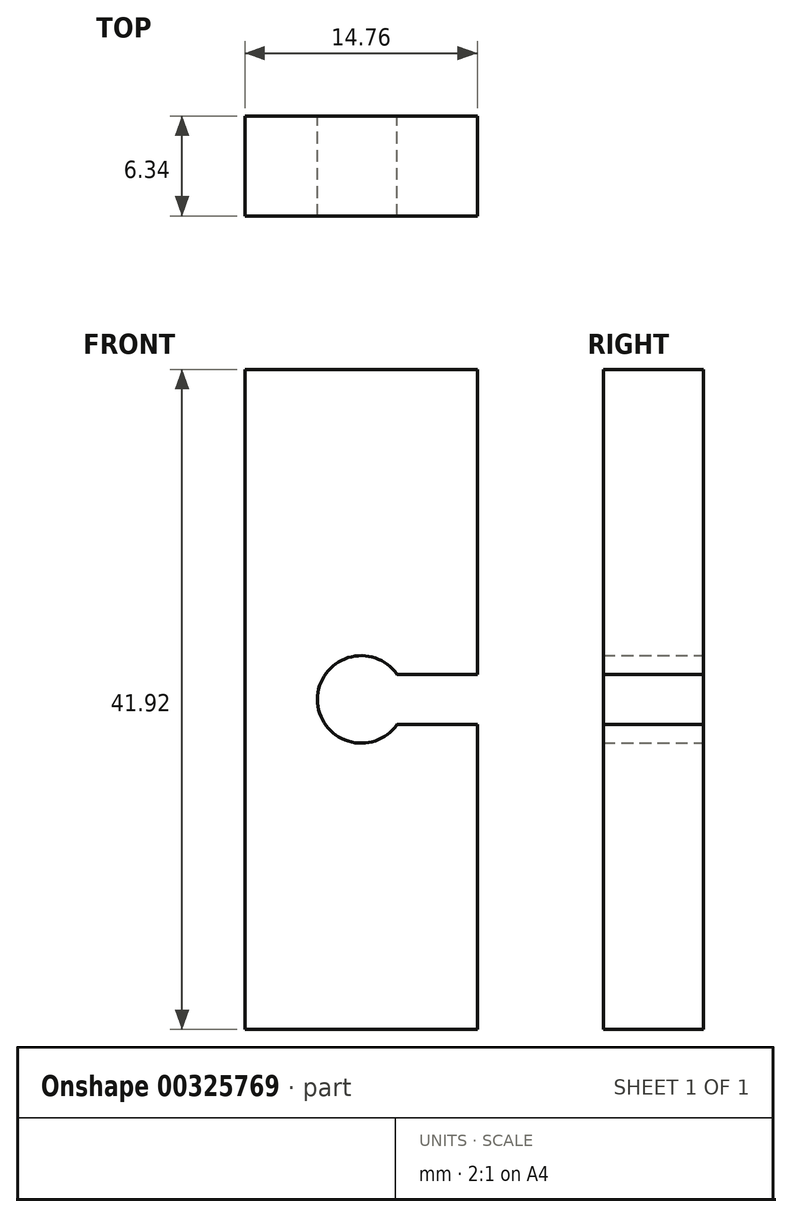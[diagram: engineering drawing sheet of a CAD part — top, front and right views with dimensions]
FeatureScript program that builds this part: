
annotation { "Feature Type Name" : "Feature", "Feature Type Description" : "" }
export const myFeature = defineFeature(function(context is Context, id is Id, definition is map)
    precondition{}
    {
        {
            var Q0;
            Q0=qCreatedBy(makeId("Front.planeOp"),FACE);
            var sketch = newSketch(context, id + "F0", { "sketchPlane" : qUnion([Q0])});
            skLineSegment(sketch, "E0.bottom", {"start": v(-7.38, 20.96) * mm, "end": v(7.38, 20.96) * mm});
            skLineSegment(sketch, "E0.top", {"start": v(-7.38, -20.96) * mm, "end": v(7.38, -20.96) * mm});
            skLineSegment(sketch, "E0.left", {"start": v(-7.38, 20.96) * mm, "end": v(-7.38, -20.96) * mm});
            skLineSegment(sketch, "E0.right", {"start": v(7.38, 20.96) * mm, "end": v(7.38, -20.96) * mm});
            skCircle(sketch, "E1", {"center": v(0, 16.51) * mm, "radius": 1.75 * mm});
            skCircle(sketch, "E2", {"center": v(0, -16.51) * mm, "radius": 1.75 * mm});
            skLineSegment(sketch, "E3", {"start": v(0, 20.96) * mm, "end": v(0, -20.96) * mm});
            skLineSegment(sketch, "E4", {"start": v(-7.38, 0) * mm, "end": v(7.38, 0) * mm});
            skCircle(sketch, "E5", {"center": v(0, 16.51) * mm, "radius": 3.18 * mm});
            skCircle(sketch, "E6.MirrorC", {"center": v(0, -16.51) * mm, "radius": 3.18 * mm});
            skCircle(sketch, "E7", {"center": v(0, 0) * mm, "radius": 2.78 * mm});
            skLineSegment(sketch, "E8.bottom", {"start": v(7.38, -1.59) * mm, "end": v(2.28, -1.59) * mm});
            skLineSegment(sketch, "E8.top", {"start": v(7.38, 1.59) * mm, "end": v(2.28, 1.59) * mm});
            skLineSegment(sketch, "E8.left", {"start": v(7.38, -1.59) * mm, "end": v(7.38, 1.59) * mm});
            skLineSegment(sketch, "E8.right", {"start": v(2.28, -1.59) * mm, "end": v(2.28, 1.59) * mm});
            skSolve(sketch);
        }
        {
            var Q0;
            {var subQ7=sQuery(id+"F0.wireOp",EDGE,"E8.top");Q0=makeQuery(id+"F0.imprint","IMPRINT",FACE,{"disambiguationData":[TD([[makeQuery(id+"F0.imprint","IMPRINT",EDGE,{"derivedFrom":subQ7}),-1.0]])]});}
            var Q1;
            {var subQ5=sQuery(id+"F0.wireOp",EDGE,"E0.bottom");var subQ8=sQuery(id+"F0.wireOp",EDGE,"E0.left");var subQ9=makeQuery(id+"F0.imprint","INTERSECT",VERTEX,{"derivedFrom":[subQ5,subQ8]});Q1=makeQuery(id+"F0.imprint","IMPRINT",FACE,{"disambiguationData":[TD([[makeQuery(id+"F0.imprint","IMPRINT",EDGE,{"disambiguationData":[TD([[subQ9,-1.0]])],"derivedFrom":subQ5}),-1.0]])]});}
            var Q2;
            {var subQ1=sQuery(id+"F0.wireOp",EDGE,"E0.top");var subQ8=sQuery(id+"F0.wireOp",EDGE,"E0.left");var subQ9=makeQuery(id+"F0.imprint","INTERSECT",VERTEX,{"derivedFrom":[subQ1,subQ8]});Q2=makeQuery(id+"F0.imprint","IMPRINT",FACE,{"disambiguationData":[TD([[makeQuery(id+"F0.imprint","IMPRINT",EDGE,{"disambiguationData":[TD([[subQ9,-1.0]])],"derivedFrom":subQ1}),1.0]])]});}
            var Q3;
            {var subQ8=sQuery(id+"F0.wireOp",EDGE,"E8.bottom");Q3=makeQuery(id+"F0.imprint","IMPRINT",FACE,{"disambiguationData":[TD([[makeQuery(id+"F0.imprint","IMPRINT",EDGE,{"derivedFrom":subQ8}),1.0]])]});}
            var Q4;
            {var subQ0=sQuery(id+"F0.wireOp",EDGE,"E3");var subQ1=sQuery(id+"F0.wireOp",EDGE,"E2");var subQ2=makeQuery(id+"F0.imprint","INTERSECT",VERTEX,{"disambiguationData":[OD(0.0)],"derivedFrom":[subQ1,subQ0]});Q4=makeQuery(id+"F0.imprint","IMPRINT",FACE,{"disambiguationData":[TD([[makeQuery(id+"F0.imprint","IMPRINT",EDGE,{"disambiguationData":[TD([[subQ2,1.0]])],"derivedFrom":subQ1}),-1.0]])]});}
            var Q5;
            {var subQ0=sQuery(id+"F0.wireOp",EDGE,"E3");var subQ1=sQuery(id+"F0.wireOp",EDGE,"E2");var subQ2=makeQuery(id+"F0.imprint","INTERSECT",VERTEX,{"disambiguationData":[OD(0.0)],"derivedFrom":[subQ1,subQ0]});Q5=makeQuery(id+"F0.imprint","IMPRINT",FACE,{"disambiguationData":[TD([[makeQuery(id+"F0.imprint","IMPRINT",EDGE,{"disambiguationData":[TD([[subQ2,-1.0]])],"derivedFrom":subQ1}),-1.0]])]});}
            var Q6;
            {var subQ0=sQuery(id+"F0.wireOp",EDGE,"E3");var subQ1=sQuery(id+"F0.wireOp",EDGE,"E1");var subQ2=makeQuery(id+"F0.imprint","INTERSECT",VERTEX,{"disambiguationData":[OD(0.0)],"derivedFrom":[subQ1,subQ0]});Q6=makeQuery(id+"F0.imprint","IMPRINT",FACE,{"disambiguationData":[TD([[makeQuery(id+"F0.imprint","IMPRINT",EDGE,{"disambiguationData":[TD([[subQ2,1.0]])],"derivedFrom":subQ1}),-1.0]])]});}
            var Q7;
            {var subQ0=sQuery(id+"F0.wireOp",EDGE,"E3");var subQ1=sQuery(id+"F0.wireOp",EDGE,"E1");var subQ2=makeQuery(id+"F0.imprint","INTERSECT",VERTEX,{"disambiguationData":[OD(0.0)],"derivedFrom":[subQ1,subQ0]});Q7=makeQuery(id+"F0.imprint","IMPRINT",FACE,{"disambiguationData":[TD([[makeQuery(id+"F0.imprint","IMPRINT",EDGE,{"disambiguationData":[TD([[subQ2,-1.0]])],"derivedFrom":subQ1}),-1.0]])]});}
            var Q8;
            {var subQ0=sQuery(id+"F0.wireOp",EDGE,"E3");var subQ1=sQuery(id+"F0.wireOp",EDGE,"E2");var subQ2=makeQuery(id+"F0.imprint","INTERSECT",VERTEX,{"disambiguationData":[OD(0.0)],"derivedFrom":[subQ1,subQ0]});Q8=makeQuery(id+"F0.imprint","IMPRINT",FACE,{"disambiguationData":[TD([[makeQuery(id+"F0.imprint","IMPRINT",EDGE,{"disambiguationData":[TD([[subQ2,-1.0]])],"derivedFrom":subQ1}),1.0]])]});}
            var Q9;
            {var subQ0=sQuery(id+"F0.wireOp",EDGE,"E3");var subQ1=sQuery(id+"F0.wireOp",EDGE,"E2");var subQ2=makeQuery(id+"F0.imprint","INTERSECT",VERTEX,{"disambiguationData":[OD(0.0)],"derivedFrom":[subQ1,subQ0]});Q9=makeQuery(id+"F0.imprint","IMPRINT",FACE,{"disambiguationData":[TD([[makeQuery(id+"F0.imprint","IMPRINT",EDGE,{"disambiguationData":[TD([[subQ2,1.0]])],"derivedFrom":subQ1}),1.0]])]});}
            var Q10;
            {var subQ0=sQuery(id+"F0.wireOp",EDGE,"E3");var subQ1=sQuery(id+"F0.wireOp",EDGE,"E1");var subQ2=makeQuery(id+"F0.imprint","INTERSECT",VERTEX,{"disambiguationData":[OD(0.0)],"derivedFrom":[subQ1,subQ0]});Q10=makeQuery(id+"F0.imprint","IMPRINT",FACE,{"disambiguationData":[TD([[makeQuery(id+"F0.imprint","IMPRINT",EDGE,{"disambiguationData":[TD([[subQ2,1.0]])],"derivedFrom":subQ1}),1.0]])]});}
            var Q11;
            {var subQ0=sQuery(id+"F0.wireOp",EDGE,"E3");var subQ1=sQuery(id+"F0.wireOp",EDGE,"E1");var subQ2=makeQuery(id+"F0.imprint","INTERSECT",VERTEX,{"disambiguationData":[OD(0.0)],"derivedFrom":[subQ1,subQ0]});Q11=makeQuery(id+"F0.imprint","IMPRINT",FACE,{"disambiguationData":[TD([[makeQuery(id+"F0.imprint","IMPRINT",EDGE,{"disambiguationData":[TD([[subQ2,-1.0]])],"derivedFrom":subQ1}),1.0]])]});}
            extrude(context, id + "F1", {"entities" : qUnion([Q0, Q1, Q2, Q3, Q4, Q5, Q6, Q7, Q8, Q9, Q10, Q11]), "endBound" : BoundingType.SYMMETRIC, "depth" : 6.35 * mm});
        }
    });
